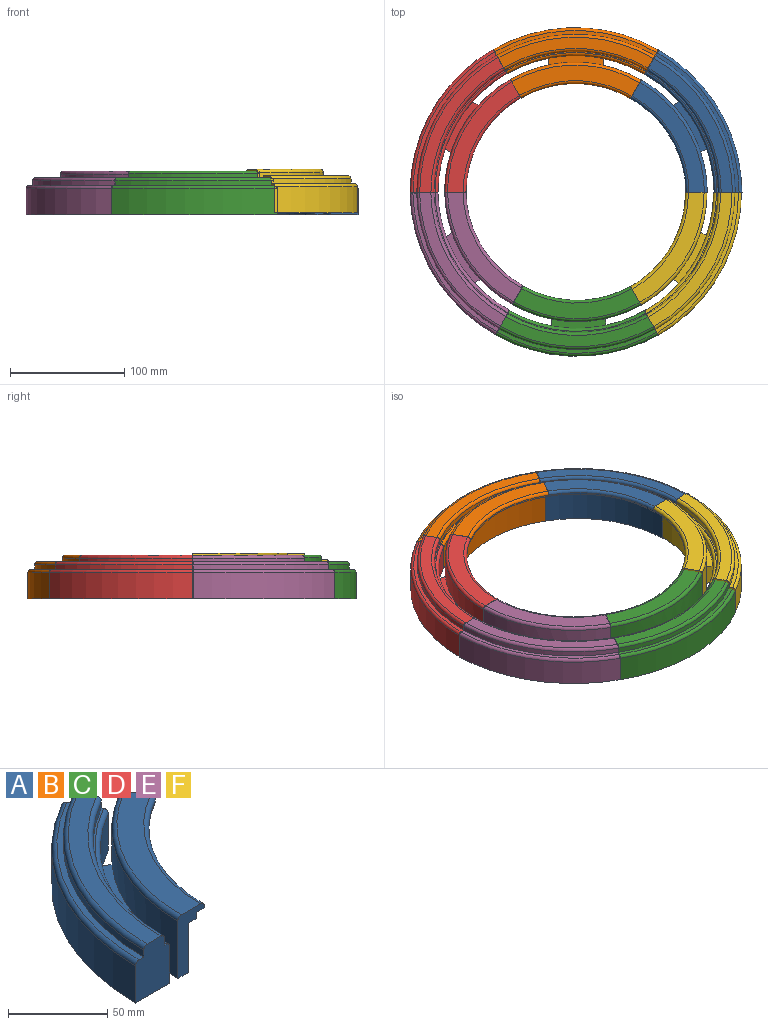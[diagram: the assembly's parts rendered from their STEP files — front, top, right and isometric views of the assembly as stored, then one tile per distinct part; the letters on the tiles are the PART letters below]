
ASSEMBLY  parts=6 mates=1
PART A: 28 faces, bbox 109x135.8x38.1 mm
  f0: cylinder r=101.25mm len=87.86mm, axis (0,0,-1), area 405.3mm2, adj f5,f17,f24,f25
  f1: cylinder r=114.37mm len=99.07mm, axis (0,0,-1), area 3424.5mm2, adj f4,f19,f20,f21,f23,f24,f25
  f2: cylinder r=95.54mm len=82.9mm, axis (0,0,1), area 127.5mm2, adj f5,f22,f24,f25
  f3: plane 96.87x63.1mm, normal (0,0,1), area 1505.1mm2, adj f22,f23,f24,f25
  f4: plane 125.41x91.46mm, normal (0,0,-1), area 4544.9mm2, adj f1,f6,f11,f18,f19,f20,f24,f25
  f5: plane 87.86x53.76mm, normal (0,0,-1), area 590.4mm2, adj f0,f2,f24,f25
  f6: cylinder r=120.15mm len=104.26mm, axis (0,0,-1), area 2041.4mm2, adj f4,f16,f19,f20,f21,f26,f27
  f7: plane 107.42x62.81mm, normal (0,0,1), area 143.2mm2, adj f8,f16,f26,f27
  f8: cylinder r=123.8mm len=107.42mm, axis (0,0,-1), area 561.6mm2, adj f7,f14,f26,f27
  f9: cylinder r=138.72mm len=120.37mm, axis (0,0,-1), area 629.3mm2, adj f12,f15,f26,f27
  f10: plane 118.17x73.38mm, normal (0,0,1), area 1357.5mm2, adj f14,f15,f26,f27
  f11: cylinder r=144.53mm len=125.41mm, axis (0,0,-1), area 3471.1mm2, adj f4,f13,f26,f27
  f12: plane 123.21x73.04mm, normal (0,0,1), area 482.6mm2, adj f9,f13,f26,f27
  f13: torus R=141.99mm, axis (0,0,1), area 602mm2, adj f11,f12,f26,f27
  f14: torus R=126.34mm, axis (0,0,1), area 522.8mm2, adj f8,f10,f26,f27
  f15: torus R=136.18mm, axis (0,0,1), area 577.6mm2, adj f9,f10,f26,f27
  f16: torus R=122.69mm, axis (0,0,1), area 507.5mm2, adj f6,f7,f26,f27
  f17: plane 92.65x56.44mm, normal (0,0,-1), area 602.9mm2, adj f0,f18,f24,f25
  f18: cylinder r=106.77mm len=92.65mm, axis (0,0,-1), area 3419mm2, adj f4,f17,f24,f25
  f19: plane 17.53x5.24mm, normal (0.5,0.87,0), area 106mm2, adj f1,f4,f6,f21
  f20: plane 17.53x5.16mm, normal (-0.5,-0.87,0), area 104.3mm2, adj f1,f4,f6,f21
  f21: plane 44.41x29.16mm, normal (0,0,1), area 283.1mm2, adj f1,f6,f19,f20
  f22: torus R=98.08mm, axis (0,0,1), area 404.3mm2, adj f2,f3,f24,f25
  f23: torus R=111.83mm, axis (0,0,1), area 475.1mm2, adj f1,f3,f24,f25
  f24: plane 38.11x18.86mm, normal (0,-1,0), area 351.6mm2, adj f0,f1,f2,f3,f4,f5,f17,f18
  f25: plane 38.11x16.17mm, normal (0.87,0.5,0), area 343.2mm2, adj f0,f1,f2,f3,f4,f5,f17,f18
  f26: plane 32.26x24.38mm, normal (0,-1,0), area 716.1mm2, adj f4,f6,f7,f8,f9,f10,f11,f12
  f27: plane 32.26x21.16mm, normal (0.87,0.5,0), area 716.1mm2, adj f4,f6,f7,f8,f9,f10,f11,f12
PART B: same geometry as A
PART C: same geometry as A
PART D: same geometry as A
PART E: same geometry as A
PART F: same geometry as A
PLACE A rot(axis=(0,0,-1),119.5deg) t=(34.73,-7.74,-21.34)mm
PLACE B rot(axis=(0,0,-1),60.2deg) t=(33.24,-7.06,-21.3)mm
PLACE C rot(axis=(0,0,1),120.6deg) t=(34.79,-5.72,-21.21)mm
PLACE D t=(33.13,-6.9,-21.34)mm
PLACE E rot(axis=(0,0,1),61.4deg) t=(33,-4.45,-21.4)mm
PLACE F rot(axis=(0,0,-1),180deg) t=(34.23,-6.46,-19.67)mm
MATE parallel B.f26 <-> D.f27  axis (-0.87,-0.5,0) through (-27.75,99.4,1.56)mm
